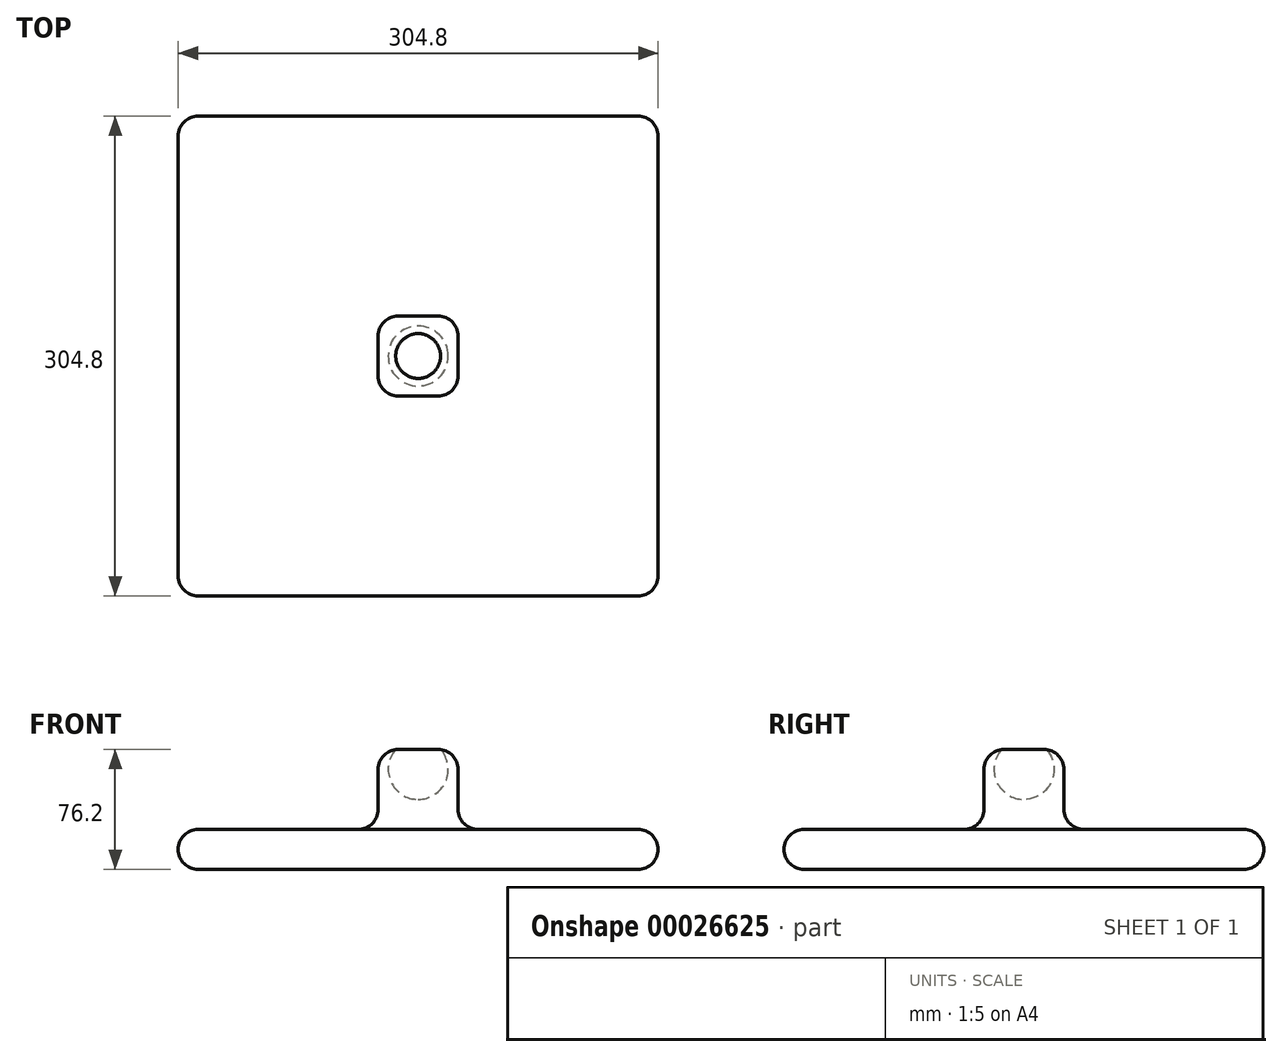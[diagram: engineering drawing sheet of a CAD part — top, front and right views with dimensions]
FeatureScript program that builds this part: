
annotation { "Feature Type Name" : "Feature", "Feature Type Description" : "" }
export const myFeature = defineFeature(function(context is Context, id is Id, definition is map)
    precondition{}
    {
        {
            var Q0;
            Q0=qCreatedBy(makeId("Front.planeOp"),FACE);
            var sketch = newSketch(context, id + "F0", { "sketchPlane" : qUnion([Q0])});
            skLineSegment(sketch, "E0.bottom", {"start": v(12.7, 0) * mm, "end": v(292.1, 0) * mm});
            skLineSegment(sketch, "E0.top", {"start": v(12.7, 25.4) * mm, "end": v(292.1, 25.4) * mm});
            skLineSegment(sketch, "E0.left", {"start": v(0, 12.7) * mm, "end": v(0, 12.7) * mm});
            skLineSegment(sketch, "E0.right", {"start": v(304.8, 12.7) * mm, "end": v(304.8, 12.7) * mm});
            skPoint(sketch, "E1.visualSharp", {"position": v(0, 25.4) * mm});
            skArc(sketch, "E1.filletArc", {"start": v(12.7, 25.4) * mm, "mid": v(3.72, 21.68) * mm, "end": v(0, 12.7) * mm});
            skPoint(sketch, "E2.visualSharp", {"position": v(0, 0) * mm});
            skArc(sketch, "E2.filletArc", {"start": v(0, 12.7) * mm, "mid": v(3.72, 3.72) * mm, "end": v(12.7, 0) * mm});
            skPoint(sketch, "E3.visualSharp", {"position": v(304.8, 0) * mm});
            skArc(sketch, "E3.filletArc", {"start": v(292.1, 0) * mm, "mid": v(301.08, 3.72) * mm, "end": v(304.8, 12.7) * mm});
            skPoint(sketch, "E4.visualSharp", {"position": v(304.8, 25.4) * mm});
            skArc(sketch, "E4.filletArc", {"start": v(304.8, 12.7) * mm, "mid": v(301.08, 21.68) * mm, "end": v(292.1, 25.4) * mm});
            skSolve(sketch);
        }
        {
            var Q0;
            Q0=makeQuery(id+"F0.imprint","IMPRINT",FACE,{"disambiguationData":[TD([[makeQuery(id+"F0.imprint","IMPRINT",EDGE,{"derivedFrom":sQuery(id+"F0.wireOp",EDGE,"E0.bottom")}),1.0]])]});
            extrude(context, id + "F1", {"entities" : qUnion([Q0]), "depth" : 304.8 * mm});
        }
        {
            var Q0;
            Q0=makeQuery(id+"F1.opExtrude","CAP_FACE",FACE,{"disambiguationData":[OSD([sQuery(id+"F0.wireOp",EDGE,"E0.bottom"),sQuery(id+"F0.wireOp",EDGE,"E0.top"),sQuery(id+"F0.wireOp",EDGE,"E1.filletArc"),sQuery(id+"F0.wireOp",EDGE,"E2.filletArc"),sQuery(id+"F0.wireOp",EDGE,"E3.filletArc"),sQuery(id+"F0.wireOp",EDGE,"E4.filletArc")])],"isStart":false});
            var Q1;
            Q1=makeQuery(id+"F1.opExtrude","CAP_FACE",FACE,{"disambiguationData":[OSD([sQuery(id+"F0.wireOp",EDGE,"E0.bottom"),sQuery(id+"F0.wireOp",EDGE,"E0.top"),sQuery(id+"F0.wireOp",EDGE,"E1.filletArc"),sQuery(id+"F0.wireOp",EDGE,"E2.filletArc"),sQuery(id+"F0.wireOp",EDGE,"E3.filletArc"),sQuery(id+"F0.wireOp",EDGE,"E4.filletArc")])],"isStart":true});
            fillet(context, id + "F2", {"entities" : qUnion([Q0, Q1]), "radius" : 12.7 * mm, "tangentPropagation" : true, "allowEdgeOverflow" : false});
        }
        {
            var Q0;
            Q0=makeQuery(id+"F1.opExtrude","SWEPT_FACE",FACE,{"disambiguationData":[OSD([sQuery(id+"F0.wireOp",EDGE,"E0.top")])]});
            var sketch = newSketch(context, id + "F3", { "sketchPlane" : qUnion([Q0])});
            skPoint(sketch, "E5", {"position": v(152.4, -292.1) * mm});
            skPoint(sketch, "E6", {"position": v(292.1, -152.4) * mm});
            skLineSegment(sketch, "E7.rect.bottom", {"start": v(177.8, -177.8) * mm, "end": v(127, -177.8) * mm});
            skLineSegment(sketch, "E7.rect.top", {"start": v(177.8, -127) * mm, "end": v(127, -127) * mm});
            skLineSegment(sketch, "E7.rect.left", {"start": v(177.8, -177.8) * mm, "end": v(177.8, -127) * mm});
            skLineSegment(sketch, "E7.rect.right", {"start": v(127, -177.8) * mm, "end": v(127, -127) * mm});
            skPoint(sketch, "E7.rect.middle", {"position": v(152.4, -152.4) * mm});
            skSolve(sketch);
        }
        {
            var Q0;
            Q0=makeQuery(id+"F3.imprint","IMPRINT",FACE,{"disambiguationData":[TD([[makeQuery(id+"F3.imprint","IMPRINT",EDGE,{"derivedFrom":sQuery(id+"F3.wireOp",EDGE,"E7.rect.bottom")}),-1.0]])]});
            extrude(context, id + "F4", {"entities" : qUnion([Q0]), "operationType" : NewBodyOperationType.ADD, "depth" : 50.8 * mm});
        }
        {
            var Q0;
            Q0=makeQuery(id+"F4.opExtrude","SWEPT_FACE",FACE,{"disambiguationData":[OSD([sQuery(id+"F3.wireOp",EDGE,"E7.rect.right")])]});
            cPlane(context, id + "F5", {"entities" : qUnion([Q0]), "cplaneType" : CPlaneType.OFFSET, "offset" : 25.4 * mm, "oppositeDirection" : true, "width" : 152.4 * mm, "height" : 152.4 * mm});
        }
        {
            var Q0;
            Q0=qCreatedBy(id+"F5.planeOp",FACE);
            var sketch = newSketch(context, id + "F6", { "sketchPlane" : qUnion([Q0])});
            skArc(sketch, "E8", {"start": v(152.4, 82.55) * mm, "mid": v(133.35, 63.5) * mm, "end": v(152.4, 44.45) * mm});
            skLineSegment(sketch, "E9", {"start": v(152.4, 63.5) * mm, "end": v(152.4, 79.9) * mm});
            skLineSegment(sketch, "E10", {"start": v(152.4, 63.5) * mm, "end": v(152.4, 44.45) * mm});
            skLineSegment(sketch, "E11", {"start": v(152.4, 44.45) * mm, "end": v(152.4, 63.5) * mm});
            skLineSegment(sketch, "E12", {"start": v(152.4, 82.55) * mm, "end": v(152.4, 63.5) * mm});
            skSolve(sketch);
        }
        {
            var Q0;
            Q0=makeQuery(id+"F4.opExtrude","SWEPT_FACE",FACE,{"disambiguationData":[OSD([sQuery(id+"F3.wireOp",EDGE,"E7.rect.bottom")])]});
            cPlane(context, id + "F7", {"entities" : qUnion([Q0]), "cplaneType" : CPlaneType.OFFSET, "offset" : 25.4 * mm, "oppositeDirection" : true, "width" : 152.4 * mm, "height" : 152.4 * mm});
        }
        {
            var Q0;
            Q0=qCreatedBy(id+"F7.planeOp",FACE);
            var sketch = newSketch(context, id + "F8", { "sketchPlane" : qUnion([Q0])});
            skLineSegment(sketch, "E13", {"start": v(152.4, 73.79) * mm, "end": v(152.4, 46.34) * mm});
            skSolve(sketch);
        }
        {
            var Q0;
            {var subQ2=sQuery(id+"F6.wireOp",EDGE,"E8");Q0=makeQuery(id+"F6.imprint","IMPRINT",FACE,{"disambiguationData":[TD([[makeQuery(id+"F6.imprint","IMPRINT",EDGE,{"derivedFrom":subQ2}),1.0]])]});}
            var Q1;
            Q1=sQuery(id+"F8.wireOp",EDGE,"E13");
            revolve(context, id + "F9", {"operationType" : NewBodyOperationType.REMOVE, "entities" : qUnion([Q0]), "axis" : qUnion([Q1]), "revolveType" : RevolveType.FULL, "oppositeDirection" : true});
        }
        {
            var Q0;
            Q0=makeQuery(id+"F4.opExtrude","SWEPT_FACE",FACE,{"disambiguationData":[OSD([sQuery(id+"F3.wireOp",EDGE,"E7.rect.left")])]});
            var Q1;
            Q1=makeQuery(id+"F4.opExtrude","SWEPT_FACE",FACE,{"disambiguationData":[OSD([sQuery(id+"F3.wireOp",EDGE,"E7.rect.top")])]});
            var Q2;
            Q2=makeQuery(id+"F4.opExtrude","SWEPT_FACE",FACE,{"disambiguationData":[OSD([sQuery(id+"F3.wireOp",EDGE,"E7.rect.bottom")])]});
            var Q3;
            Q3=makeQuery(id+"F4.opExtrude","SWEPT_FACE",FACE,{"disambiguationData":[OSD([sQuery(id+"F3.wireOp",EDGE,"E7.rect.right")])]});
            fillet(context, id + "F10", {"entities" : qUnion([Q0, Q1, Q2, Q3]), "radius" : 12.7 * mm, "tangentPropagation" : true, "allowEdgeOverflow" : false});
        }
    });
